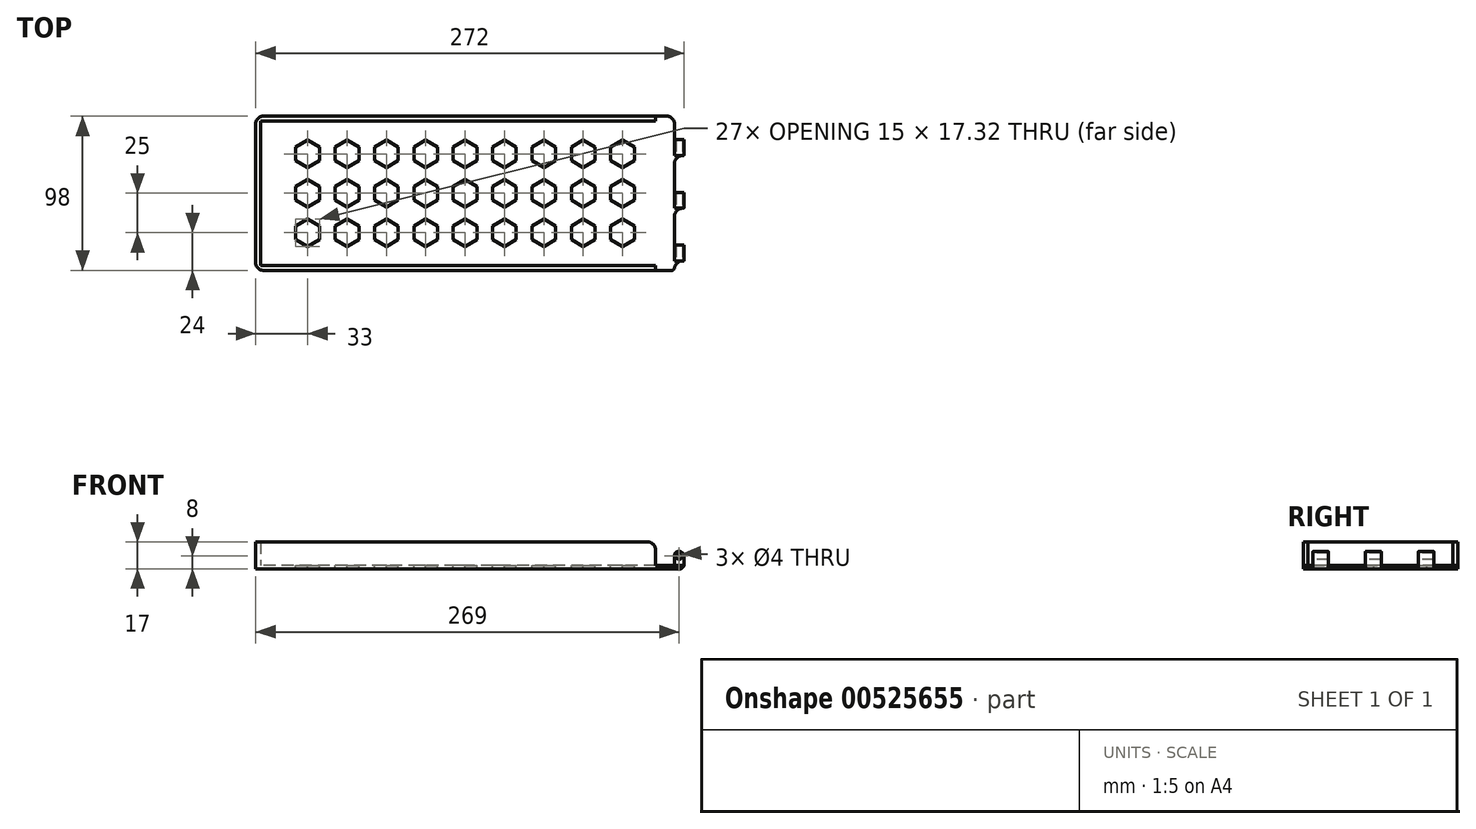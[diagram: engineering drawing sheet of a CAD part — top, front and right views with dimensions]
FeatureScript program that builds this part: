
annotation { "Feature Type Name" : "Feature", "Feature Type Description" : "" }
export const myFeature = defineFeature(function(context is Context, id is Id, definition is map)
    precondition{}
    {
        {
            var Q0;
            Q0=qCreatedBy(makeId("Top.planeOp"),FACE);
            var sketch = newSketch(context, id + "F0", { "sketchPlane" : qUnion([Q0])});
            skLineSegment(sketch, "E0.bottom", {"start": v(133, 49) * mm, "end": v(-133, 49) * mm});
            skLineSegment(sketch, "E0.top", {"start": v(133, -49) * mm, "end": v(-133, -49) * mm});
            skLineSegment(sketch, "E0.left", {"start": v(133, 49) * mm, "end": v(133, -49) * mm});
            skLineSegment(sketch, "E0.right", {"start": v(-133, 49) * mm, "end": v(-133, -49) * mm});
            skPoint(sketch, "E0.middle", {"position": v(0, 0) * mm});
            skLineSegment(sketch, "E1.bottom", {"start": v(133, -43) * mm, "end": v(139, -43) * mm});
            skLineSegment(sketch, "E1.top", {"start": v(133, -33) * mm, "end": v(139, -33) * mm});
            skLineSegment(sketch, "E1.left", {"start": v(133, -43) * mm, "end": v(133, -33) * mm});
            skLineSegment(sketch, "E1.right", {"start": v(139, -43) * mm, "end": v(139, -33) * mm});
            skLineSegment(sketch, "E2.bottom", {"start": v(133, -9.5) * mm, "end": v(139, -9.5) * mm});
            skLineSegment(sketch, "E2.top", {"start": v(133, 0.5) * mm, "end": v(139, 0.5) * mm});
            skLineSegment(sketch, "E2.left", {"start": v(133, -9.5) * mm, "end": v(133, 0.5) * mm});
            skLineSegment(sketch, "E2.right", {"start": v(139, -9.5) * mm, "end": v(139, 0.5) * mm});
            skLineSegment(sketch, "E3.bottom", {"start": v(133, 24) * mm, "end": v(139, 24) * mm});
            skLineSegment(sketch, "E3.top", {"start": v(133, 34) * mm, "end": v(139, 34) * mm});
            skLineSegment(sketch, "E3.left", {"start": v(133, 24) * mm, "end": v(133, 34) * mm});
            skLineSegment(sketch, "E3.right", {"start": v(139, 24) * mm, "end": v(139, 34) * mm});
            skSolve(sketch);
        }
        {
            var Q0;
            {var subQ6=sQuery(id+"F0.wireOp",EDGE,"E0.bottom");Q0=makeQuery(id+"F0.imprint","IMPRINT",FACE,{"disambiguationData":[TD([[makeQuery(id+"F0.imprint","IMPRINT",EDGE,{"derivedFrom":subQ6}),1.0]])]});}
            var Q1;
            {var subQ0=sQuery(id+"F0.wireOp",EDGE,"E3.bottom");Q1=makeQuery(id+"F0.imprint","IMPRINT",FACE,{"disambiguationData":[TD([[makeQuery(id+"F0.imprint","IMPRINT",EDGE,{"derivedFrom":subQ0}),1.0]])]});}
            var Q2;
            {var subQ0=sQuery(id+"F0.wireOp",EDGE,"E2.bottom");Q2=makeQuery(id+"F0.imprint","IMPRINT",FACE,{"disambiguationData":[TD([[makeQuery(id+"F0.imprint","IMPRINT",EDGE,{"derivedFrom":subQ0}),1.0]])]});}
            var Q3;
            {var subQ0=sQuery(id+"F0.wireOp",EDGE,"E1.bottom");Q3=makeQuery(id+"F0.imprint","IMPRINT",FACE,{"disambiguationData":[TD([[makeQuery(id+"F0.imprint","IMPRINT",EDGE,{"derivedFrom":subQ0}),1.0]])]});}
            extrude(context, id + "F1", {"entities" : qUnion([Q0, Q1, Q2, Q3]), "depth" : 2 * mm, "offsetDistance" : 25 * mm});
        }
        {
            var Q0;
            {var subQ0=sQuery(id+"F0.wireOp",EDGE,"E3.bottom");Q0=makeQuery(id+"F0.imprint","IMPRINT",FACE,{"disambiguationData":[TD([[makeQuery(id+"F0.imprint","IMPRINT",EDGE,{"derivedFrom":subQ0}),1.0]])]});}
            var Q1;
            {var subQ0=sQuery(id+"F0.wireOp",EDGE,"E2.bottom");Q1=makeQuery(id+"F0.imprint","IMPRINT",FACE,{"disambiguationData":[TD([[makeQuery(id+"F0.imprint","IMPRINT",EDGE,{"derivedFrom":subQ0}),1.0]])]});}
            var Q2;
            {var subQ0=sQuery(id+"F0.wireOp",EDGE,"E1.bottom");Q2=makeQuery(id+"F0.imprint","IMPRINT",FACE,{"disambiguationData":[TD([[makeQuery(id+"F0.imprint","IMPRINT",EDGE,{"derivedFrom":subQ0}),1.0]])]});}
            extrude(context, id + "F2", {"entities" : qUnion([Q0, Q1, Q2]), "operationType" : NewBodyOperationType.ADD, "depth" : 11 * mm, "offsetDistance" : 25 * mm});
        }
        {
            var Q0;
            Q0=makeQuery(id+"F1.opExtrude","CAP_FACE",FACE,{"disambiguationData":[OSD([sQuery(id+"F0.wireOp",EDGE,"E0.bottom"),sQuery(id+"F0.wireOp",EDGE,"E0.top"),sQuery(id+"F0.wireOp",EDGE,"E0.left"),sQuery(id+"F0.wireOp",EDGE,"E0.right"),sQuery(id+"F0.wireOp",EDGE,"E1.bottom"),sQuery(id+"F0.wireOp",EDGE,"E1.top"),sQuery(id+"F0.wireOp",EDGE,"E1.right"),sQuery(id+"F0.wireOp",EDGE,"E2.bottom"),sQuery(id+"F0.wireOp",EDGE,"E2.top"),sQuery(id+"F0.wireOp",EDGE,"E2.right"),sQuery(id+"F0.wireOp",EDGE,"E3.bottom"),sQuery(id+"F0.wireOp",EDGE,"E3.top"),sQuery(id+"F0.wireOp",EDGE,"E3.right")])],"isStart":false});
            var sketch = newSketch(context, id + "F3", { "sketchPlane" : qUnion([Q0])});
            skLineSegment(sketch, "E4.bottom", {"start": v(130, 46) * mm, "end": v(-130, 46) * mm});
            skLineSegment(sketch, "E4.top", {"start": v(130, -46) * mm, "end": v(-130, -46) * mm});
            skLineSegment(sketch, "E4.left", {"start": v(130, 46) * mm, "end": v(130, -46) * mm});
            skLineSegment(sketch, "E4.right", {"start": v(-130, 46) * mm, "end": v(-130, -46) * mm});
            skPoint(sketch, "E4.middle", {"position": v(0, 0) * mm});
            skLineSegment(sketch, "E5", {"start": v(130, 46) * mm, "end": v(133, 46) * mm});
            skLineSegment(sketch, "E6", {"start": v(130, -46) * mm, "end": v(133, -46) * mm});
            skLineSegment(sketch, "E7", {"start": v(121, 49) * mm, "end": v(121, -49) * mm});
            skSolve(sketch);
        }
        {
            var Q0;
            {var subQ0=sQuery(id+"F3.wireOp",EDGE,"E4.right");Q0=makeQuery(id+"F3.imprint","IMPRINT",FACE,{"disambiguationData":[TD([[makeQuery(id+"F3.imprint","IMPRINT",EDGE,{"derivedFrom":subQ0}),-1.0]])]});}
            extrude(context, id + "F4", {"entities" : qUnion([Q0]), "operationType" : NewBodyOperationType.ADD, "depth" : 15 * mm, "offsetDistance" : 25 * mm});
        }
        {
            var Q0;
            {var subQ0=sQuery(id+"F0.wireOp",EDGE,"E1.bottom");Q0=makeQuery(id+"F2.boolean.opBoolean","MERGE",FACE,{"derivedFrom":[makeQuery(id+"F1.opExtrude","SWEPT_FACE",FACE,{"disambiguationData":[OSD([subQ0])]}),makeQuery(id+"F2.opExtrude","SWEPT_FACE",FACE,{"disambiguationData":[OSD([subQ0])]})]});}
            var sketch = newSketch(context, id + "F5", { "sketchPlane" : qUnion([Q0])});
            skCircle(sketch, "E8", {"center": v(136, 8) * mm, "radius": 2 * mm});
            skSolve(sketch);
        }
        {
            var Q0;
            Q0=makeQuery(id+"F5.imprint","IMPRINT",FACE,{"disambiguationData":[TD([[makeQuery(id+"F5.imprint","IMPRINT",EDGE,{"derivedFrom":sQuery(id+"F5.wireOp",EDGE,"E8")}),1.0]])]});
            extrude(context, id + "F6", {"entities" : qUnion([Q0]), "operationType" : NewBodyOperationType.REMOVE, "endBound" : BoundingType.THROUGH_ALL, "oppositeDirection" : true, "depth" : 25 * mm, "offsetDistance" : 25 * mm});
        }
        {
            var Q0;
            Q0=makeQuery(id+"F2.opExtrude","CAP_EDGE",EDGE,{"disambiguationData":[OSD([sQuery(id+"F0.wireOp",EDGE,"E1.right")])],"isStart":false});
            var Q1;
            Q1=makeQuery(id+"F2.opExtrude","CAP_EDGE",EDGE,{"disambiguationData":[OSD([sQuery(id+"F0.wireOp",EDGE,"E2.right")])],"isStart":false});
            var Q2;
            Q2=makeQuery(id+"F2.opExtrude","CAP_EDGE",EDGE,{"disambiguationData":[OSD([sQuery(id+"F0.wireOp",EDGE,"E3.right")])],"isStart":false});
            chamfer(context, id + "F7", {"entities" : qUnion([Q0, Q1, Q2]), "width" : 2 * mm, "tangentPropagation" : true});
        }
        {
            var Q0;
            {var subQ0=sQuery(id+"F0.wireOp",EDGE,"E0.left");Q0=makeQuery(id+"F2.opExtrude","CAP_EDGE",EDGE,{"disambiguationData":[OSD([subQ0]),TDD([makeQuery(id+"F0.imprint","IMPRINT",EDGE,{"disambiguationData":[TD([[makeQuery(id+"F0.imprint","INTERSECT",VERTEX,{"derivedFrom":[subQ0,sQuery(id+"F0.wireOp",EDGE,"E1.bottom")]}),1.0]])],"derivedFrom":subQ0})])],"isStart":false});}
            var Q1;
            {var subQ0=sQuery(id+"F0.wireOp",EDGE,"E0.left");Q1=makeQuery(id+"F2.opExtrude","CAP_EDGE",EDGE,{"disambiguationData":[OSD([subQ0]),TDD([makeQuery(id+"F0.imprint","IMPRINT",EDGE,{"disambiguationData":[TD([[makeQuery(id+"F0.imprint","INTERSECT",VERTEX,{"derivedFrom":[subQ0,sQuery(id+"F0.wireOp",EDGE,"E2.bottom")]}),1.0]])],"derivedFrom":subQ0})])],"isStart":false});}
            var Q2;
            {var subQ0=sQuery(id+"F0.wireOp",EDGE,"E0.left");Q2=makeQuery(id+"F2.opExtrude","CAP_EDGE",EDGE,{"disambiguationData":[OSD([subQ0]),TDD([makeQuery(id+"F0.imprint","IMPRINT",EDGE,{"disambiguationData":[TD([[makeQuery(id+"F0.imprint","INTERSECT",VERTEX,{"derivedFrom":[subQ0,sQuery(id+"F0.wireOp",EDGE,"E3.bottom")]}),1.0]])],"derivedFrom":subQ0})])],"isStart":false});}
            var Q3;
            Q3=makeQuery(id+"F1.opExtrude","CAP_EDGE",EDGE,{"disambiguationData":[OSD([sQuery(id+"F0.wireOp",EDGE,"E3.right")])],"isStart":true});
            var Q4;
            Q4=makeQuery(id+"F1.opExtrude","CAP_EDGE",EDGE,{"disambiguationData":[OSD([sQuery(id+"F0.wireOp",EDGE,"E2.right")])],"isStart":true});
            var Q5;
            Q5=makeQuery(id+"F1.opExtrude","CAP_EDGE",EDGE,{"disambiguationData":[OSD([sQuery(id+"F0.wireOp",EDGE,"E1.right")])],"isStart":true});
            var Q6;
            {var subQ0=sQuery(id+"F0.wireOp",EDGE,"E1.right");Q6=makeQuery(id+"F7.opChamfer","BLEND_EDGE",EDGE,{"blendedFrom":[makeQuery(id+"F2.opExtrude","CAP_EDGE",EDGE,{"disambiguationData":[OSD([subQ0])],"isStart":false}),makeQuery(id+"F2.boolean.opBoolean","MERGE",FACE,{"derivedFrom":[makeQuery(id+"F1.opExtrude","SWEPT_FACE",FACE,{"disambiguationData":[OSD([subQ0])]}),makeQuery(id+"F2.opExtrude","SWEPT_FACE",FACE,{"disambiguationData":[OSD([subQ0])]})]})],"blendedInto":[makeQuery(id+"F2.boolean.opBoolean","MERGE",FACE,{"derivedFrom":[makeQuery(id+"F1.opExtrude","SWEPT_FACE",FACE,{"disambiguationData":[OSD([subQ0])]}),makeQuery(id+"F2.opExtrude","SWEPT_FACE",FACE,{"disambiguationData":[OSD([subQ0])]})]})]});}
            var Q7;
            {var subQ0=sQuery(id+"F0.wireOp",EDGE,"E2.right");Q7=makeQuery(id+"F7.opChamfer","BLEND_EDGE",EDGE,{"blendedFrom":[makeQuery(id+"F2.opExtrude","CAP_EDGE",EDGE,{"disambiguationData":[OSD([subQ0])],"isStart":false}),makeQuery(id+"F2.boolean.opBoolean","MERGE",FACE,{"derivedFrom":[makeQuery(id+"F1.opExtrude","SWEPT_FACE",FACE,{"disambiguationData":[OSD([subQ0])]}),makeQuery(id+"F2.opExtrude","SWEPT_FACE",FACE,{"disambiguationData":[OSD([subQ0])]})]})],"blendedInto":[makeQuery(id+"F2.boolean.opBoolean","MERGE",FACE,{"derivedFrom":[makeQuery(id+"F1.opExtrude","SWEPT_FACE",FACE,{"disambiguationData":[OSD([subQ0])]}),makeQuery(id+"F2.opExtrude","SWEPT_FACE",FACE,{"disambiguationData":[OSD([subQ0])]})]})]});}
            var Q8;
            {var subQ0=sQuery(id+"F0.wireOp",EDGE,"E3.right");Q8=makeQuery(id+"F7.opChamfer","BLEND_EDGE",EDGE,{"blendedFrom":[makeQuery(id+"F2.opExtrude","CAP_EDGE",EDGE,{"disambiguationData":[OSD([subQ0])],"isStart":false}),makeQuery(id+"F2.boolean.opBoolean","MERGE",FACE,{"derivedFrom":[makeQuery(id+"F1.opExtrude","SWEPT_FACE",FACE,{"disambiguationData":[OSD([subQ0])]}),makeQuery(id+"F2.opExtrude","SWEPT_FACE",FACE,{"disambiguationData":[OSD([subQ0])]})]})],"blendedInto":[makeQuery(id+"F2.boolean.opBoolean","MERGE",FACE,{"derivedFrom":[makeQuery(id+"F1.opExtrude","SWEPT_FACE",FACE,{"disambiguationData":[OSD([subQ0])]}),makeQuery(id+"F2.opExtrude","SWEPT_FACE",FACE,{"disambiguationData":[OSD([subQ0])]})]})]});}
            var Q9;
            {var subQ0=sQuery(id+"F0.wireOp",EDGE,"E1.right");Q9=makeQuery(id+"F7.opChamfer","BLEND_EDGE",EDGE,{"blendedFrom":[makeQuery(id+"F2.opExtrude","CAP_EDGE",EDGE,{"disambiguationData":[OSD([subQ0])],"isStart":false}),makeQuery(id+"F2.opExtrude","CAP_FACE",FACE,{"disambiguationData":[OSD([sQuery(id+"F0.wireOp",EDGE,"E0.left"),sQuery(id+"F0.wireOp",EDGE,"E1.bottom"),sQuery(id+"F0.wireOp",EDGE,"E1.top"),subQ0])],"isStart":false})],"blendedInto":[makeQuery(id+"F2.opExtrude","CAP_FACE",FACE,{"disambiguationData":[OSD([sQuery(id+"F0.wireOp",EDGE,"E0.left"),sQuery(id+"F0.wireOp",EDGE,"E1.bottom"),sQuery(id+"F0.wireOp",EDGE,"E1.top"),subQ0])],"isStart":false})]});}
            var Q10;
            {var subQ0=sQuery(id+"F0.wireOp",EDGE,"E2.right");Q10=makeQuery(id+"F7.opChamfer","BLEND_EDGE",EDGE,{"blendedFrom":[makeQuery(id+"F2.opExtrude","CAP_EDGE",EDGE,{"disambiguationData":[OSD([subQ0])],"isStart":false}),makeQuery(id+"F2.opExtrude","CAP_FACE",FACE,{"disambiguationData":[OSD([sQuery(id+"F0.wireOp",EDGE,"E0.left"),sQuery(id+"F0.wireOp",EDGE,"E2.bottom"),sQuery(id+"F0.wireOp",EDGE,"E2.top"),subQ0])],"isStart":false})],"blendedInto":[makeQuery(id+"F2.opExtrude","CAP_FACE",FACE,{"disambiguationData":[OSD([sQuery(id+"F0.wireOp",EDGE,"E0.left"),sQuery(id+"F0.wireOp",EDGE,"E2.bottom"),sQuery(id+"F0.wireOp",EDGE,"E2.top"),subQ0])],"isStart":false})]});}
            var Q11;
            {var subQ0=sQuery(id+"F0.wireOp",EDGE,"E3.right");Q11=makeQuery(id+"F7.opChamfer","BLEND_EDGE",EDGE,{"blendedFrom":[makeQuery(id+"F2.opExtrude","CAP_EDGE",EDGE,{"disambiguationData":[OSD([subQ0])],"isStart":false}),makeQuery(id+"F2.opExtrude","CAP_FACE",FACE,{"disambiguationData":[OSD([sQuery(id+"F0.wireOp",EDGE,"E0.left"),sQuery(id+"F0.wireOp",EDGE,"E3.bottom"),sQuery(id+"F0.wireOp",EDGE,"E3.top"),subQ0])],"isStart":false})],"blendedInto":[makeQuery(id+"F2.opExtrude","CAP_FACE",FACE,{"disambiguationData":[OSD([sQuery(id+"F0.wireOp",EDGE,"E0.left"),sQuery(id+"F0.wireOp",EDGE,"E3.bottom"),sQuery(id+"F0.wireOp",EDGE,"E3.top"),subQ0])],"isStart":false})]});}
            fillet(context, id + "F8", {"entities" : qUnion([Q0, Q1, Q2, Q3, Q4, Q5, Q6, Q7, Q8, Q9, Q10, Q11]), "radius" : 2.5 * mm, "tangentPropagation" : true, "allowEdgeOverflow" : false});
        }
        {
            var Q0;
            {var subQ0=sQuery(id+"F0.wireOp",EDGE,"E0.right");var subQ1=sQuery(id+"F0.wireOp",EDGE,"E0.top");Q0=makeQuery(id+"F4.boolean.opBoolean","MERGE",EDGE,{"derivedFrom":[makeQuery(id+"F1.opExtrude","SWEPT_EDGE",EDGE,{"disambiguationData":[OSD([subQ1,subQ0])]}),makeQuery(id+"F4.opExtrude","SWEPT_EDGE",EDGE,{"disambiguationData":[OSD([subQ1,subQ0])]})]});}
            var Q1;
            {var subQ0=sQuery(id+"F0.wireOp",EDGE,"E0.right");var subQ1=sQuery(id+"F0.wireOp",EDGE,"E0.bottom");Q1=makeQuery(id+"F4.boolean.opBoolean","MERGE",EDGE,{"derivedFrom":[makeQuery(id+"F1.opExtrude","SWEPT_EDGE",EDGE,{"disambiguationData":[OSD([subQ1,subQ0])]}),makeQuery(id+"F4.opExtrude","SWEPT_EDGE",EDGE,{"disambiguationData":[OSD([subQ1,subQ0])]})]});}
            var Q2;
            {var subQ0=sQuery(id+"F0.wireOp",EDGE,"E0.right");var subQ1=sQuery(id+"F0.wireOp",EDGE,"E0.bottom");Q2=makeQuery(id+"F4.boolean.opBoolean","MERGE",EDGE,{"derivedFrom":[makeQuery(id+"F1.opExtrude","SWEPT_EDGE",EDGE,{"disambiguationData":[OSD([subQ1,subQ0])]}),makeQuery(id+"F4.opExtrude","SWEPT_EDGE",EDGE,{"disambiguationData":[OSD([subQ1,subQ0])]})]});}
            fillet(context, id + "F9", {"entities" : qUnion([Q0, Q1, Q2]), "radius" : 5 * mm, "tangentPropagation" : true, "allowEdgeOverflow" : false});
        }
        {
            var Q0;
            Q0=makeQuery(id+"F1.opExtrude","SWEPT_EDGE",EDGE,{"disambiguationData":[OSD([sQuery(id+"F0.wireOp",EDGE,"E0.left"),sQuery(id+"F0.wireOp",EDGE,"E1.bottom")])]});
            var Q1;
            Q1=makeQuery(id+"F1.opExtrude","SWEPT_EDGE",EDGE,{"disambiguationData":[OSD([sQuery(id+"F0.wireOp",EDGE,"E0.left"),sQuery(id+"F0.wireOp",EDGE,"E2.bottom")])]});
            var Q2;
            Q2=makeQuery(id+"F1.opExtrude","SWEPT_EDGE",EDGE,{"disambiguationData":[OSD([sQuery(id+"F0.wireOp",EDGE,"E0.left"),sQuery(id+"F0.wireOp",EDGE,"E3.bottom")])]});
            var Q3;
            Q3=makeQuery(id+"F1.opExtrude","SWEPT_EDGE",EDGE,{"disambiguationData":[OSD([sQuery(id+"F0.wireOp",EDGE,"E0.bottom"),sQuery(id+"F0.wireOp",EDGE,"E0.left")])]});
            var Q4;
            {var subQ0=sQuery(id+"F3.wireOp",EDGE,"E7");Q4=makeQuery(id+"F4.opExtrude","CAP_EDGE",EDGE,{"disambiguationData":[OSD([subQ0]),TDD([makeQuery(id+"F3.imprint","IMPRINT",EDGE,{"disambiguationData":[TD([[makeQuery(id+"F3.imprint","INTERSECT",VERTEX,{"derivedFrom":[makeQuery(id+"F1.opExtrude","CAP_EDGE",EDGE,{"disambiguationData":[OSD([sQuery(id+"F0.wireOp",EDGE,"E0.top")])],"isStart":false}),subQ0]}),1.0]])],"derivedFrom":subQ0})])],"isStart":false});}
            var Q5;
            {var subQ0=sQuery(id+"F3.wireOp",EDGE,"E7");Q5=makeQuery(id+"F4.opExtrude","CAP_EDGE",EDGE,{"disambiguationData":[OSD([subQ0]),TDD([makeQuery(id+"F3.imprint","IMPRINT",EDGE,{"disambiguationData":[TD([[makeQuery(id+"F3.imprint","INTERSECT",VERTEX,{"derivedFrom":[makeQuery(id+"F1.opExtrude","CAP_EDGE",EDGE,{"disambiguationData":[OSD([sQuery(id+"F0.wireOp",EDGE,"E0.bottom")])],"isStart":false}),subQ0]}),-1.0]])],"derivedFrom":subQ0})])],"isStart":false});}
            fillet(context, id + "F10", {"entities" : qUnion([Q0, Q1, Q2, Q3, Q4, Q5]), "radius" : 5 * mm, "tangentPropagation" : true, "allowEdgeOverflow" : false});
        }
        {
            var Q0;
            Q0=makeQuery(id+"F1.opExtrude","SWEPT_EDGE",EDGE,{"disambiguationData":[OSD([sQuery(id+"F0.wireOp",EDGE,"E0.top"),sQuery(id+"F0.wireOp",EDGE,"E0.left")])]});
            fillet(context, id + "F11", {"entities" : qUnion([Q0]), "radius" : 2 * mm, "tangentPropagation" : true, "allowEdgeOverflow" : false});
        }
        {
            var Q0;
            Q0=makeQuery(id+"F1.opExtrude","CAP_FACE",FACE,{"disambiguationData":[OSD([sQuery(id+"F0.wireOp",EDGE,"E0.bottom"),sQuery(id+"F0.wireOp",EDGE,"E0.top"),sQuery(id+"F0.wireOp",EDGE,"E0.left"),sQuery(id+"F0.wireOp",EDGE,"E0.right"),sQuery(id+"F0.wireOp",EDGE,"E1.bottom"),sQuery(id+"F0.wireOp",EDGE,"E1.top"),sQuery(id+"F0.wireOp",EDGE,"E1.right"),sQuery(id+"F0.wireOp",EDGE,"E2.bottom"),sQuery(id+"F0.wireOp",EDGE,"E2.top"),sQuery(id+"F0.wireOp",EDGE,"E2.right"),sQuery(id+"F0.wireOp",EDGE,"E3.bottom"),sQuery(id+"F0.wireOp",EDGE,"E3.top"),sQuery(id+"F0.wireOp",EDGE,"E3.right")])],"isStart":false});
            var sketch = newSketch(context, id + "F12", { "sketchPlane" : qUnion([Q0])});
            skCircle(sketch, "E9.cCircle", {"center": v(0, 0) * mm, "radius": 7.5 * mm, "construction": true});
            skLineSegment(sketch, "E9.0", {"start": v(7.5, 4.33) * mm, "end": v(7.5, -4.33) * mm});
            skLineSegment(sketch, "E9.1", {"start": v(7.5, -4.33) * mm, "end": v(0, -8.66) * mm});
            skLineSegment(sketch, "E9.2", {"start": v(0, -8.66) * mm, "end": v(-7.5, -4.33) * mm});
            skLineSegment(sketch, "E9.3", {"start": v(-7.5, -4.33) * mm, "end": v(-7.5, 4.33) * mm});
            skLineSegment(sketch, "E9.4", {"start": v(-7.5, 4.33) * mm, "end": v(0, 8.66) * mm});
            skLineSegment(sketch, "E9.5", {"start": v(0, 8.66) * mm, "end": v(7.5, 4.33) * mm});
            skPoint(sketch, "E9.0.midPoint", {"position": v(7.5, 0) * mm});
            skLineSegment(sketch, "E10.0.1.0", {"start": v(7.5, 20.67) * mm, "end": v(0, 16.34) * mm});
            skCircle(sketch, "E10.0.1.1", {"center": v(0, 25) * mm, "radius": 7.5 * mm, "construction": true});
            skPoint(sketch, "E10.0.1.2", {"position": v(7.5, 25) * mm});
            skLineSegment(sketch, "E10.0.1.3", {"start": v(0, 33.66) * mm, "end": v(7.5, 29.33) * mm});
            skLineSegment(sketch, "E10.0.1.4", {"start": v(0, 16.34) * mm, "end": v(-7.5, 20.67) * mm});
            skLineSegment(sketch, "E10.0.1.5", {"start": v(7.5, 29.33) * mm, "end": v(7.5, 20.67) * mm});
            skLineSegment(sketch, "E10.0.1.6", {"start": v(-7.5, 29.33) * mm, "end": v(0, 33.66) * mm});
            skLineSegment(sketch, "E10.0.1.7", {"start": v(-7.5, 20.67) * mm, "end": v(-7.5, 29.33) * mm});
            skLineSegment(sketch, "E10.direction1", {"start": v(-7.5, -4.33) * mm, "end": v(17.5, -4.33) * mm, "construction": true});
            skLineSegment(sketch, "E10.direction2", {"start": v(-7.5, -4.33) * mm, "end": v(-7.5, 20.67) * mm, "construction": true});
            skLineSegment(sketch, "E11.0.1.0", {"start": v(-7.5, -29.33) * mm, "end": v(-7.5, -20.67) * mm});
            skPoint(sketch, "E11.0.1.1", {"position": v(7.5, -25) * mm});
            skCircle(sketch, "E11.0.1.2", {"center": v(0, -25) * mm, "radius": 7.5 * mm, "construction": true});
            skLineSegment(sketch, "E11.0.1.3", {"start": v(0, -16.34) * mm, "end": v(7.5, -20.67) * mm});
            skLineSegment(sketch, "E11.0.1.4", {"start": v(-7.5, -20.67) * mm, "end": v(0, -16.34) * mm});
            skLineSegment(sketch, "E11.0.1.5", {"start": v(0, -33.66) * mm, "end": v(-7.5, -29.33) * mm});
            skLineSegment(sketch, "E11.0.1.6", {"start": v(7.5, -20.67) * mm, "end": v(7.5, -29.33) * mm});
            skLineSegment(sketch, "E11.0.1.7", {"start": v(7.5, -29.33) * mm, "end": v(0, -33.66) * mm});
            skLineSegment(sketch, "E11.direction2", {"start": v(-7.5, -4.33) * mm, "end": v(-7.5, -29.33) * mm, "construction": true});
            skLineSegment(sketch, "E12.1.0.0", {"start": v(17.5, -4.33) * mm, "end": v(17.5, -29.33) * mm, "construction": true});
            skPoint(sketch, "E12.1.0.1", {"position": v(32.5, -25) * mm});
            skPoint(sketch, "E12.1.0.2", {"position": v(32.5, 25) * mm});
            skLineSegment(sketch, "E12.1.0.3", {"start": v(17.5, -4.33) * mm, "end": v(17.5, 20.67) * mm, "construction": true});
            skPoint(sketch, "E12.1.0.4", {"position": v(32.5, 0) * mm});
            skLineSegment(sketch, "E12.1.0.5", {"start": v(17.5, -20.67) * mm, "end": v(25, -16.34) * mm});
            skLineSegment(sketch, "E12.1.0.6", {"start": v(32.5, -29.33) * mm, "end": v(25, -33.66) * mm});
            skLineSegment(sketch, "E12.1.0.7", {"start": v(32.5, 29.33) * mm, "end": v(32.5, 20.67) * mm});
            skLineSegment(sketch, "E12.1.0.8", {"start": v(25, 16.34) * mm, "end": v(17.5, 20.67) * mm});
            skLineSegment(sketch, "E12.1.0.9", {"start": v(17.5, 20.67) * mm, "end": v(17.5, 29.33) * mm});
            skCircle(sketch, "E12.1.0.10", {"center": v(25, 0) * mm, "radius": 7.5 * mm, "construction": true});
            skLineSegment(sketch, "E12.1.0.11", {"start": v(32.5, 4.33) * mm, "end": v(32.5, -4.33) * mm});
            skLineSegment(sketch, "E12.1.0.12", {"start": v(32.5, -4.33) * mm, "end": v(25, -8.66) * mm});
            skLineSegment(sketch, "E12.1.0.13", {"start": v(25, -8.66) * mm, "end": v(17.5, -4.33) * mm});
            skLineSegment(sketch, "E12.1.0.14", {"start": v(25, 33.66) * mm, "end": v(32.5, 29.33) * mm});
            skLineSegment(sketch, "E12.1.0.15", {"start": v(32.5, 20.67) * mm, "end": v(25, 16.34) * mm});
            skLineSegment(sketch, "E12.1.0.16", {"start": v(25, 8.66) * mm, "end": v(32.5, 4.33) * mm});
            skCircle(sketch, "E12.1.0.17", {"center": v(25, -25) * mm, "radius": 7.5 * mm, "construction": true});
            skLineSegment(sketch, "E12.1.0.18", {"start": v(17.5, 4.33) * mm, "end": v(25, 8.66) * mm});
            skLineSegment(sketch, "E12.1.0.19", {"start": v(25, -16.34) * mm, "end": v(32.5, -20.67) * mm});
            skLineSegment(sketch, "E12.1.0.20", {"start": v(32.5, -20.67) * mm, "end": v(32.5, -29.33) * mm});
            skLineSegment(sketch, "E12.1.0.21", {"start": v(17.5, 29.33) * mm, "end": v(25, 33.66) * mm});
            skLineSegment(sketch, "E12.1.0.22", {"start": v(25, -33.66) * mm, "end": v(17.5, -29.33) * mm});
            skLineSegment(sketch, "E12.1.0.23", {"start": v(17.5, -4.33) * mm, "end": v(17.5, 4.33) * mm});
            skLineSegment(sketch, "E12.1.0.24", {"start": v(17.5, -29.33) * mm, "end": v(17.5, -20.67) * mm});
            skCircle(sketch, "E12.1.0.25", {"center": v(25, 25) * mm, "radius": 7.5 * mm, "construction": true});
            skLineSegment(sketch, "E12.2.0.0", {"start": v(42.5, -4.33) * mm, "end": v(42.5, -29.33) * mm, "construction": true});
            skPoint(sketch, "E12.2.0.1", {"position": v(57.5, -25) * mm});
            skPoint(sketch, "E12.2.0.2", {"position": v(57.5, 25) * mm});
            skLineSegment(sketch, "E12.2.0.3", {"start": v(42.5, -4.33) * mm, "end": v(42.5, 20.67) * mm, "construction": true});
            skPoint(sketch, "E12.2.0.4", {"position": v(57.5, 0) * mm});
            skLineSegment(sketch, "E12.2.0.5", {"start": v(42.5, -20.67) * mm, "end": v(50, -16.34) * mm});
            skLineSegment(sketch, "E12.2.0.6", {"start": v(57.5, -29.33) * mm, "end": v(50, -33.66) * mm});
            skLineSegment(sketch, "E12.2.0.7", {"start": v(57.5, 29.33) * mm, "end": v(57.5, 20.67) * mm});
            skLineSegment(sketch, "E12.2.0.8", {"start": v(50, 16.34) * mm, "end": v(42.5, 20.67) * mm});
            skLineSegment(sketch, "E12.2.0.9", {"start": v(42.5, 20.67) * mm, "end": v(42.5, 29.33) * mm});
            skCircle(sketch, "E12.2.0.10", {"center": v(50, 0) * mm, "radius": 7.5 * mm, "construction": true});
            skLineSegment(sketch, "E12.2.0.11", {"start": v(57.5, 4.33) * mm, "end": v(57.5, -4.33) * mm});
            skLineSegment(sketch, "E12.2.0.12", {"start": v(57.5, -4.33) * mm, "end": v(50, -8.66) * mm});
            skLineSegment(sketch, "E12.2.0.13", {"start": v(50, -8.66) * mm, "end": v(42.5, -4.33) * mm});
            skLineSegment(sketch, "E12.2.0.14", {"start": v(50, 33.66) * mm, "end": v(57.5, 29.33) * mm});
            skLineSegment(sketch, "E12.2.0.15", {"start": v(57.5, 20.67) * mm, "end": v(50, 16.34) * mm});
            skLineSegment(sketch, "E12.2.0.16", {"start": v(50, 8.66) * mm, "end": v(57.5, 4.33) * mm});
            skCircle(sketch, "E12.2.0.17", {"center": v(50, -25) * mm, "radius": 7.5 * mm, "construction": true});
            skLineSegment(sketch, "E12.2.0.18", {"start": v(42.5, 4.33) * mm, "end": v(50, 8.66) * mm});
            skLineSegment(sketch, "E12.2.0.19", {"start": v(50, -16.34) * mm, "end": v(57.5, -20.67) * mm});
            skLineSegment(sketch, "E12.2.0.20", {"start": v(57.5, -20.67) * mm, "end": v(57.5, -29.33) * mm});
            skLineSegment(sketch, "E12.2.0.21", {"start": v(42.5, 29.33) * mm, "end": v(50, 33.66) * mm});
            skLineSegment(sketch, "E12.2.0.22", {"start": v(50, -33.66) * mm, "end": v(42.5, -29.33) * mm});
            skLineSegment(sketch, "E12.2.0.23", {"start": v(42.5, -4.33) * mm, "end": v(42.5, 4.33) * mm});
            skLineSegment(sketch, "E12.2.0.24", {"start": v(42.5, -29.33) * mm, "end": v(42.5, -20.67) * mm});
            skCircle(sketch, "E12.2.0.25", {"center": v(50, 25) * mm, "radius": 7.5 * mm, "construction": true});
            skLineSegment(sketch, "E12.3.0.0", {"start": v(67.5, -4.33) * mm, "end": v(67.5, -29.33) * mm, "construction": true});
            skPoint(sketch, "E12.3.0.1", {"position": v(82.5, -25) * mm});
            skPoint(sketch, "E12.3.0.2", {"position": v(82.5, 25) * mm});
            skLineSegment(sketch, "E12.3.0.3", {"start": v(67.5, -4.33) * mm, "end": v(67.5, 20.67) * mm, "construction": true});
            skPoint(sketch, "E12.3.0.4", {"position": v(82.5, 0) * mm});
            skLineSegment(sketch, "E12.3.0.5", {"start": v(67.5, -20.67) * mm, "end": v(75, -16.34) * mm});
            skLineSegment(sketch, "E12.3.0.6", {"start": v(82.5, -29.33) * mm, "end": v(75, -33.66) * mm});
            skLineSegment(sketch, "E12.3.0.7", {"start": v(82.5, 29.33) * mm, "end": v(82.5, 20.67) * mm});
            skLineSegment(sketch, "E12.3.0.8", {"start": v(75, 16.34) * mm, "end": v(67.5, 20.67) * mm});
            skLineSegment(sketch, "E12.3.0.9", {"start": v(67.5, 20.67) * mm, "end": v(67.5, 29.33) * mm});
            skCircle(sketch, "E12.3.0.10", {"center": v(75, 0) * mm, "radius": 7.5 * mm, "construction": true});
            skLineSegment(sketch, "E12.3.0.11", {"start": v(82.5, 4.33) * mm, "end": v(82.5, -4.33) * mm});
            skLineSegment(sketch, "E12.3.0.12", {"start": v(82.5, -4.33) * mm, "end": v(75, -8.66) * mm});
            skLineSegment(sketch, "E12.3.0.13", {"start": v(75, -8.66) * mm, "end": v(67.5, -4.33) * mm});
            skLineSegment(sketch, "E12.3.0.14", {"start": v(75, 33.66) * mm, "end": v(82.5, 29.33) * mm});
            skLineSegment(sketch, "E12.3.0.15", {"start": v(82.5, 20.67) * mm, "end": v(75, 16.34) * mm});
            skLineSegment(sketch, "E12.3.0.16", {"start": v(75, 8.66) * mm, "end": v(82.5, 4.33) * mm});
            skCircle(sketch, "E12.3.0.17", {"center": v(75, -25) * mm, "radius": 7.5 * mm, "construction": true});
            skLineSegment(sketch, "E12.3.0.18", {"start": v(67.5, 4.33) * mm, "end": v(75, 8.66) * mm});
            skLineSegment(sketch, "E12.3.0.19", {"start": v(75, -16.34) * mm, "end": v(82.5, -20.67) * mm});
            skLineSegment(sketch, "E12.3.0.20", {"start": v(82.5, -20.67) * mm, "end": v(82.5, -29.33) * mm});
            skLineSegment(sketch, "E12.3.0.21", {"start": v(67.5, 29.33) * mm, "end": v(75, 33.66) * mm});
            skLineSegment(sketch, "E12.3.0.22", {"start": v(75, -33.66) * mm, "end": v(67.5, -29.33) * mm});
            skLineSegment(sketch, "E12.3.0.23", {"start": v(67.5, -4.33) * mm, "end": v(67.5, 4.33) * mm});
            skLineSegment(sketch, "E12.3.0.24", {"start": v(67.5, -29.33) * mm, "end": v(67.5, -20.67) * mm});
            skCircle(sketch, "E12.3.0.25", {"center": v(75, 25) * mm, "radius": 7.5 * mm, "construction": true});
            skLineSegment(sketch, "E12.4.0.0", {"start": v(92.5, -4.33) * mm, "end": v(92.5, -29.33) * mm, "construction": true});
            skPoint(sketch, "E12.4.0.1", {"position": v(107.5, -25) * mm});
            skPoint(sketch, "E12.4.0.2", {"position": v(107.5, 25) * mm});
            skLineSegment(sketch, "E12.4.0.3", {"start": v(92.5, -4.33) * mm, "end": v(92.5, 20.67) * mm, "construction": true});
            skPoint(sketch, "E12.4.0.4", {"position": v(107.5, 0) * mm});
            skLineSegment(sketch, "E12.4.0.5", {"start": v(92.5, -20.67) * mm, "end": v(100, -16.34) * mm});
            skLineSegment(sketch, "E12.4.0.6", {"start": v(107.5, -29.33) * mm, "end": v(100, -33.66) * mm});
            skLineSegment(sketch, "E12.4.0.7", {"start": v(107.5, 29.33) * mm, "end": v(107.5, 20.67) * mm});
            skLineSegment(sketch, "E12.4.0.8", {"start": v(100, 16.34) * mm, "end": v(92.5, 20.67) * mm});
            skLineSegment(sketch, "E12.4.0.9", {"start": v(92.5, 20.67) * mm, "end": v(92.5, 29.33) * mm});
            skCircle(sketch, "E12.4.0.10", {"center": v(100, 0) * mm, "radius": 7.5 * mm, "construction": true});
            skLineSegment(sketch, "E12.4.0.11", {"start": v(107.5, 4.33) * mm, "end": v(107.5, -4.33) * mm});
            skLineSegment(sketch, "E12.4.0.12", {"start": v(107.5, -4.33) * mm, "end": v(100, -8.66) * mm});
            skLineSegment(sketch, "E12.4.0.13", {"start": v(100, -8.66) * mm, "end": v(92.5, -4.33) * mm});
            skLineSegment(sketch, "E12.4.0.14", {"start": v(100, 33.66) * mm, "end": v(107.5, 29.33) * mm});
            skLineSegment(sketch, "E12.4.0.15", {"start": v(107.5, 20.67) * mm, "end": v(100, 16.34) * mm});
            skLineSegment(sketch, "E12.4.0.16", {"start": v(100, 8.66) * mm, "end": v(107.5, 4.33) * mm});
            skCircle(sketch, "E12.4.0.17", {"center": v(100, -25) * mm, "radius": 7.5 * mm, "construction": true});
            skLineSegment(sketch, "E12.4.0.18", {"start": v(92.5, 4.33) * mm, "end": v(100, 8.66) * mm});
            skLineSegment(sketch, "E12.4.0.19", {"start": v(100, -16.34) * mm, "end": v(107.5, -20.67) * mm});
            skLineSegment(sketch, "E12.4.0.20", {"start": v(107.5, -20.67) * mm, "end": v(107.5, -29.33) * mm});
            skLineSegment(sketch, "E12.4.0.21", {"start": v(92.5, 29.33) * mm, "end": v(100, 33.66) * mm});
            skLineSegment(sketch, "E12.4.0.22", {"start": v(100, -33.66) * mm, "end": v(92.5, -29.33) * mm});
            skLineSegment(sketch, "E12.4.0.23", {"start": v(92.5, -4.33) * mm, "end": v(92.5, 4.33) * mm});
            skLineSegment(sketch, "E12.4.0.24", {"start": v(92.5, -29.33) * mm, "end": v(92.5, -20.67) * mm});
            skCircle(sketch, "E12.4.0.25", {"center": v(100, 25) * mm, "radius": 7.5 * mm, "construction": true});
            skLineSegment(sketch, "E12.direction1", {"start": v(-7.5, -29.33) * mm, "end": v(17.5, -29.33) * mm, "construction": true});
            skPoint(sketch, "E13.1.0.0", {"position": v(-17.5, 0) * mm});
            skLineSegment(sketch, "E13.1.0.1", {"start": v(-32.5, -4.33) * mm, "end": v(-32.5, 20.67) * mm, "construction": true});
            skCircle(sketch, "E13.1.0.2", {"center": v(-25, 25) * mm, "radius": 7.5 * mm, "construction": true});
            skCircle(sketch, "E13.1.0.3", {"center": v(-25, 0) * mm, "radius": 7.5 * mm, "construction": true});
            skLineSegment(sketch, "E13.1.0.4", {"start": v(-32.5, 20.67) * mm, "end": v(-32.5, 29.33) * mm});
            skCircle(sketch, "E13.1.0.5", {"center": v(-25, -25) * mm, "radius": 7.5 * mm, "construction": true});
            skPoint(sketch, "E13.1.0.6", {"position": v(-17.5, 25) * mm});
            skLineSegment(sketch, "E13.1.0.7", {"start": v(-32.5, -4.33) * mm, "end": v(-32.5, -29.33) * mm, "construction": true});
            skPoint(sketch, "E13.1.0.8", {"position": v(-17.5, -25) * mm});
            skLineSegment(sketch, "E13.1.0.9", {"start": v(-32.5, -29.33) * mm, "end": v(-32.5, -20.67) * mm});
            skLineSegment(sketch, "E13.1.0.10", {"start": v(-17.5, -20.67) * mm, "end": v(-17.5, -29.33) * mm});
            skLineSegment(sketch, "E13.1.0.11", {"start": v(-17.5, 29.33) * mm, "end": v(-17.5, 20.67) * mm});
            skLineSegment(sketch, "E13.1.0.12", {"start": v(-32.5, 4.33) * mm, "end": v(-25, 8.66) * mm});
            skLineSegment(sketch, "E13.1.0.13", {"start": v(-25, -8.66) * mm, "end": v(-32.5, -4.33) * mm});
            skLineSegment(sketch, "E13.1.0.14", {"start": v(-17.5, -4.33) * mm, "end": v(-25, -8.66) * mm});
            skLineSegment(sketch, "E13.1.0.15", {"start": v(-17.5, -29.33) * mm, "end": v(-25, -33.66) * mm});
            skLineSegment(sketch, "E13.1.0.16", {"start": v(-32.5, 29.33) * mm, "end": v(-25, 33.66) * mm});
            skLineSegment(sketch, "E13.1.0.17", {"start": v(-25, 16.34) * mm, "end": v(-32.5, 20.67) * mm});
            skLineSegment(sketch, "E13.1.0.18", {"start": v(-25, 33.66) * mm, "end": v(-17.5, 29.33) * mm});
            skLineSegment(sketch, "E13.1.0.19", {"start": v(-17.5, 20.67) * mm, "end": v(-25, 16.34) * mm});
            skLineSegment(sketch, "E13.1.0.20", {"start": v(-25, 8.66) * mm, "end": v(-17.5, 4.33) * mm});
            skLineSegment(sketch, "E13.1.0.21", {"start": v(-32.5, -4.33) * mm, "end": v(-32.5, 4.33) * mm});
            skLineSegment(sketch, "E13.1.0.22", {"start": v(-17.5, 4.33) * mm, "end": v(-17.5, -4.33) * mm});
            skLineSegment(sketch, "E13.1.0.23", {"start": v(-25, -33.66) * mm, "end": v(-32.5, -29.33) * mm});
            skLineSegment(sketch, "E13.1.0.24", {"start": v(-25, -16.34) * mm, "end": v(-17.5, -20.67) * mm});
            skLineSegment(sketch, "E13.1.0.25", {"start": v(-32.5, -20.67) * mm, "end": v(-25, -16.34) * mm});
            skPoint(sketch, "E13.2.0.0", {"position": v(-42.5, 0) * mm});
            skLineSegment(sketch, "E13.2.0.1", {"start": v(-57.5, -4.33) * mm, "end": v(-57.5, 20.67) * mm, "construction": true});
            skCircle(sketch, "E13.2.0.2", {"center": v(-50, 25) * mm, "radius": 7.5 * mm, "construction": true});
            skCircle(sketch, "E13.2.0.3", {"center": v(-50, 0) * mm, "radius": 7.5 * mm, "construction": true});
            skLineSegment(sketch, "E13.2.0.4", {"start": v(-57.5, 20.67) * mm, "end": v(-57.5, 29.33) * mm});
            skCircle(sketch, "E13.2.0.5", {"center": v(-50, -25) * mm, "radius": 7.5 * mm, "construction": true});
            skPoint(sketch, "E13.2.0.6", {"position": v(-42.5, 25) * mm});
            skLineSegment(sketch, "E13.2.0.7", {"start": v(-57.5, -4.33) * mm, "end": v(-57.5, -29.33) * mm, "construction": true});
            skPoint(sketch, "E13.2.0.8", {"position": v(-42.5, -25) * mm});
            skLineSegment(sketch, "E13.2.0.9", {"start": v(-57.5, -29.33) * mm, "end": v(-57.5, -20.67) * mm});
            skLineSegment(sketch, "E13.2.0.10", {"start": v(-42.5, -20.67) * mm, "end": v(-42.5, -29.33) * mm});
            skLineSegment(sketch, "E13.2.0.11", {"start": v(-42.5, 29.33) * mm, "end": v(-42.5, 20.67) * mm});
            skLineSegment(sketch, "E13.2.0.12", {"start": v(-57.5, 4.33) * mm, "end": v(-50, 8.66) * mm});
            skLineSegment(sketch, "E13.2.0.13", {"start": v(-50, -8.66) * mm, "end": v(-57.5, -4.33) * mm});
            skLineSegment(sketch, "E13.2.0.14", {"start": v(-42.5, -4.33) * mm, "end": v(-50, -8.66) * mm});
            skLineSegment(sketch, "E13.2.0.15", {"start": v(-42.5, -29.33) * mm, "end": v(-50, -33.66) * mm});
            skLineSegment(sketch, "E13.2.0.16", {"start": v(-57.5, 29.33) * mm, "end": v(-50, 33.66) * mm});
            skLineSegment(sketch, "E13.2.0.17", {"start": v(-50, 16.34) * mm, "end": v(-57.5, 20.67) * mm});
            skLineSegment(sketch, "E13.2.0.18", {"start": v(-50, 33.66) * mm, "end": v(-42.5, 29.33) * mm});
            skLineSegment(sketch, "E13.2.0.19", {"start": v(-42.5, 20.67) * mm, "end": v(-50, 16.34) * mm});
            skLineSegment(sketch, "E13.2.0.20", {"start": v(-50, 8.66) * mm, "end": v(-42.5, 4.33) * mm});
            skLineSegment(sketch, "E13.2.0.21", {"start": v(-57.5, -4.33) * mm, "end": v(-57.5, 4.33) * mm});
            skLineSegment(sketch, "E13.2.0.22", {"start": v(-42.5, 4.33) * mm, "end": v(-42.5, -4.33) * mm});
            skLineSegment(sketch, "E13.2.0.23", {"start": v(-50, -33.66) * mm, "end": v(-57.5, -29.33) * mm});
            skLineSegment(sketch, "E13.2.0.24", {"start": v(-50, -16.34) * mm, "end": v(-42.5, -20.67) * mm});
            skLineSegment(sketch, "E13.2.0.25", {"start": v(-57.5, -20.67) * mm, "end": v(-50, -16.34) * mm});
            skPoint(sketch, "E13.3.0.0", {"position": v(-67.5, 0) * mm});
            skLineSegment(sketch, "E13.3.0.1", {"start": v(-82.5, -4.33) * mm, "end": v(-82.5, 20.67) * mm, "construction": true});
            skCircle(sketch, "E13.3.0.2", {"center": v(-75, 25) * mm, "radius": 7.5 * mm, "construction": true});
            skCircle(sketch, "E13.3.0.3", {"center": v(-75, 0) * mm, "radius": 7.5 * mm, "construction": true});
            skLineSegment(sketch, "E13.3.0.4", {"start": v(-82.5, 20.67) * mm, "end": v(-82.5, 29.33) * mm});
            skCircle(sketch, "E13.3.0.5", {"center": v(-75, -25) * mm, "radius": 7.5 * mm, "construction": true});
            skPoint(sketch, "E13.3.0.6", {"position": v(-67.5, 25) * mm});
            skLineSegment(sketch, "E13.3.0.7", {"start": v(-82.5, -4.33) * mm, "end": v(-82.5, -29.33) * mm, "construction": true});
            skPoint(sketch, "E13.3.0.8", {"position": v(-67.5, -25) * mm});
            skLineSegment(sketch, "E13.3.0.9", {"start": v(-82.5, -29.33) * mm, "end": v(-82.5, -20.67) * mm});
            skLineSegment(sketch, "E13.3.0.10", {"start": v(-67.5, -20.67) * mm, "end": v(-67.5, -29.33) * mm});
            skLineSegment(sketch, "E13.3.0.11", {"start": v(-67.5, 29.33) * mm, "end": v(-67.5, 20.67) * mm});
            skLineSegment(sketch, "E13.3.0.12", {"start": v(-82.5, 4.33) * mm, "end": v(-75, 8.66) * mm});
            skLineSegment(sketch, "E13.3.0.13", {"start": v(-75, -8.66) * mm, "end": v(-82.5, -4.33) * mm});
            skLineSegment(sketch, "E13.3.0.14", {"start": v(-67.5, -4.33) * mm, "end": v(-75, -8.66) * mm});
            skLineSegment(sketch, "E13.3.0.15", {"start": v(-67.5, -29.33) * mm, "end": v(-75, -33.66) * mm});
            skLineSegment(sketch, "E13.3.0.16", {"start": v(-82.5, 29.33) * mm, "end": v(-75, 33.66) * mm});
            skLineSegment(sketch, "E13.3.0.17", {"start": v(-75, 16.34) * mm, "end": v(-82.5, 20.67) * mm});
            skLineSegment(sketch, "E13.3.0.18", {"start": v(-75, 33.66) * mm, "end": v(-67.5, 29.33) * mm});
            skLineSegment(sketch, "E13.3.0.19", {"start": v(-67.5, 20.67) * mm, "end": v(-75, 16.34) * mm});
            skLineSegment(sketch, "E13.3.0.20", {"start": v(-75, 8.66) * mm, "end": v(-67.5, 4.33) * mm});
            skLineSegment(sketch, "E13.3.0.21", {"start": v(-82.5, -4.33) * mm, "end": v(-82.5, 4.33) * mm});
            skLineSegment(sketch, "E13.3.0.22", {"start": v(-67.5, 4.33) * mm, "end": v(-67.5, -4.33) * mm});
            skLineSegment(sketch, "E13.3.0.23", {"start": v(-75, -33.66) * mm, "end": v(-82.5, -29.33) * mm});
            skLineSegment(sketch, "E13.3.0.24", {"start": v(-75, -16.34) * mm, "end": v(-67.5, -20.67) * mm});
            skLineSegment(sketch, "E13.3.0.25", {"start": v(-82.5, -20.67) * mm, "end": v(-75, -16.34) * mm});
            skPoint(sketch, "E13.4.0.0", {"position": v(-92.5, 0) * mm});
            skLineSegment(sketch, "E13.4.0.1", {"start": v(-107.5, -4.33) * mm, "end": v(-107.5, 20.67) * mm, "construction": true});
            skCircle(sketch, "E13.4.0.2", {"center": v(-100, 25) * mm, "radius": 7.5 * mm, "construction": true});
            skCircle(sketch, "E13.4.0.3", {"center": v(-100, 0) * mm, "radius": 7.5 * mm, "construction": true});
            skLineSegment(sketch, "E13.4.0.4", {"start": v(-107.5, 20.67) * mm, "end": v(-107.5, 29.33) * mm});
            skCircle(sketch, "E13.4.0.5", {"center": v(-100, -25) * mm, "radius": 7.5 * mm, "construction": true});
            skPoint(sketch, "E13.4.0.6", {"position": v(-92.5, 25) * mm});
            skLineSegment(sketch, "E13.4.0.7", {"start": v(-107.5, -4.33) * mm, "end": v(-107.5, -29.33) * mm, "construction": true});
            skPoint(sketch, "E13.4.0.8", {"position": v(-92.5, -25) * mm});
            skLineSegment(sketch, "E13.4.0.9", {"start": v(-107.5, -29.33) * mm, "end": v(-107.5, -20.67) * mm});
            skLineSegment(sketch, "E13.4.0.10", {"start": v(-92.5, -20.67) * mm, "end": v(-92.5, -29.33) * mm});
            skLineSegment(sketch, "E13.4.0.11", {"start": v(-92.5, 29.33) * mm, "end": v(-92.5, 20.67) * mm});
            skLineSegment(sketch, "E13.4.0.12", {"start": v(-107.5, 4.33) * mm, "end": v(-100, 8.66) * mm});
            skLineSegment(sketch, "E13.4.0.13", {"start": v(-100, -8.66) * mm, "end": v(-107.5, -4.33) * mm});
            skLineSegment(sketch, "E13.4.0.14", {"start": v(-92.5, -4.33) * mm, "end": v(-100, -8.66) * mm});
            skLineSegment(sketch, "E13.4.0.15", {"start": v(-92.5, -29.33) * mm, "end": v(-100, -33.66) * mm});
            skLineSegment(sketch, "E13.4.0.16", {"start": v(-107.5, 29.33) * mm, "end": v(-100, 33.66) * mm});
            skLineSegment(sketch, "E13.4.0.17", {"start": v(-100, 16.34) * mm, "end": v(-107.5, 20.67) * mm});
            skLineSegment(sketch, "E13.4.0.18", {"start": v(-100, 33.66) * mm, "end": v(-92.5, 29.33) * mm});
            skLineSegment(sketch, "E13.4.0.19", {"start": v(-92.5, 20.67) * mm, "end": v(-100, 16.34) * mm});
            skLineSegment(sketch, "E13.4.0.20", {"start": v(-100, 8.66) * mm, "end": v(-92.5, 4.33) * mm});
            skLineSegment(sketch, "E13.4.0.21", {"start": v(-107.5, -4.33) * mm, "end": v(-107.5, 4.33) * mm});
            skLineSegment(sketch, "E13.4.0.22", {"start": v(-92.5, 4.33) * mm, "end": v(-92.5, -4.33) * mm});
            skLineSegment(sketch, "E13.4.0.23", {"start": v(-100, -33.66) * mm, "end": v(-107.5, -29.33) * mm});
            skLineSegment(sketch, "E13.4.0.24", {"start": v(-100, -16.34) * mm, "end": v(-92.5, -20.67) * mm});
            skLineSegment(sketch, "E13.4.0.25", {"start": v(-107.5, -20.67) * mm, "end": v(-100, -16.34) * mm});
            skLineSegment(sketch, "E13.direction1", {"start": v(-7.5, -29.33) * mm, "end": v(-32.5, -29.33) * mm, "construction": true});
            skSolve(sketch);
        }
        {
            var Q0;
            Q0 = qSketchRegion(id + "F12", true);
            extrude(context, id + "F13", {"entities" : qUnion([Q0]), "operationType" : NewBodyOperationType.REMOVE, "oppositeDirection" : true, "depth" : 25 * mm, "offsetDistance" : 25 * mm});
        }
    });
